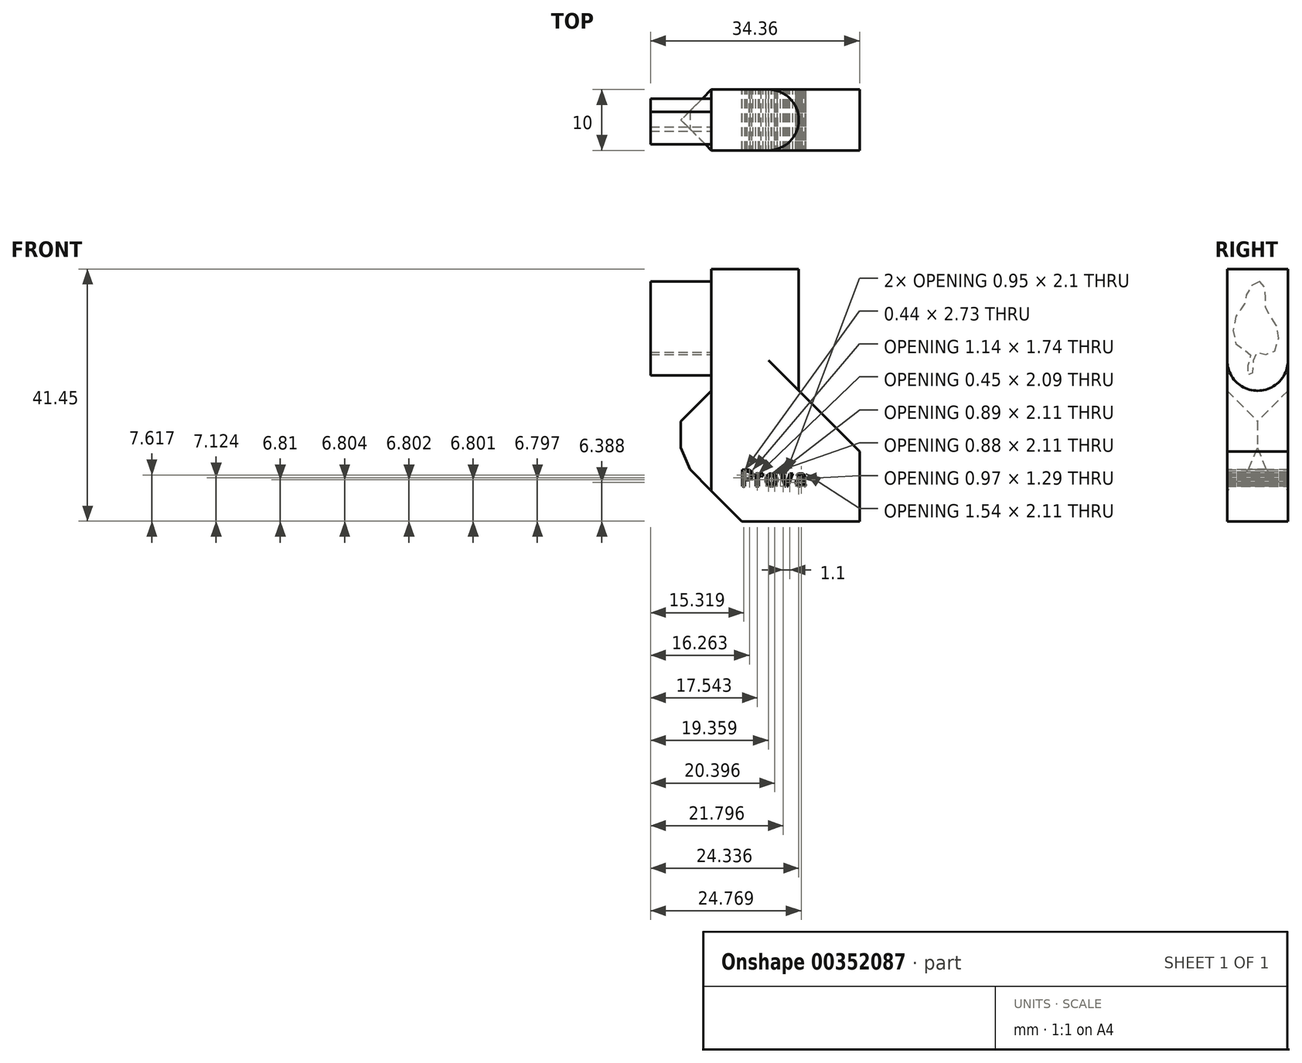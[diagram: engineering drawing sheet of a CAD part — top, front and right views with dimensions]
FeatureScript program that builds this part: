
annotation { "Feature Type Name" : "Feature", "Feature Type Description" : "" }
export const myFeature = defineFeature(function(context is Context, id is Id, definition is map)
    precondition{}
    {
        {
            var Q0;
            Q0=qCreatedBy(makeId("Front.planeOp"),FACE);
            var sketch = newSketch(context, id + "F0", { "sketchPlane" : qUnion([Q0])});
            skLineSegment(sketch, "E0.bottom", {"start": v(0, 30.39) * mm, "end": v(29.36, 30.39) * mm});
            skLineSegment(sketch, "E0.top", {"start": v(0, 8.94) * mm, "end": v(29.36, 8.94) * mm});
            skLineSegment(sketch, "E0.left", {"start": v(0, 30.39) * mm, "end": v(0, 8.94) * mm});
            skLineSegment(sketch, "E0.right", {"start": v(29.36, 30.39) * mm, "end": v(29.36, 8.94) * mm});
            skLineSegment(sketch, "E1", {"start": v(29.36, 21.93) * mm, "end": v(43.85, 8.6) * mm});
            skLineSegment(sketch, "E2", {"start": v(43.85, 8.6) * mm, "end": v(29.36, 8.94) * mm});
            skLineSegment(sketch, "E3", {"start": v(-10.64, 19.66) * mm, "end": v(0, 19.66) * mm});
            skPoint(sketch, "E3.startSnap0", {"position": v(0, 19.66) * mm});
            skLineSegment(sketch, "E4", {"start": v(0, 19.66) * mm, "end": v(-10.64, 19.66) * mm});
            skLineSegment(sketch, "E5", {"start": v(-10.64, 19.66) * mm, "end": v(-10.64, 15.53) * mm});
            skLineSegment(sketch, "E6", {"start": v(-10.64, 15.53) * mm, "end": v(-4.86, 15.53) * mm});
            skLineSegment(sketch, "E7", {"start": v(-4.86, 15.53) * mm, "end": v(-4.86, 12.5) * mm});
            skLineSegment(sketch, "E8", {"start": v(-4.86, 12.5) * mm, "end": v(-12.4, 9.66) * mm});
            skLineSegment(sketch, "E9", {"start": v(-12.4, 9.66) * mm, "end": v(0, 8.94) * mm});
            skText(sketch, "E10", { "text": "Prova", "fontName": "AllertaStencil-Regular.ttf"});
            const initialGuessF0  = {"E10": [0.00976, 0.0147, 1, 0, 0.00273]};
            skSetInitialGuess(sketch, initialGuessF0);
            skSolve(sketch);
        }
        {
            var Q0;
            {var subQ3=sQuery(id+"F0.wireOp",EDGE,"E0.bottom");Q0=makeQuery(id+"F0.imprint","IMPRINT",FACE,{"disambiguationData":[TD([[makeQuery(id+"F0.imprint","IMPRINT",EDGE,{"derivedFrom":subQ3}),-1.0]])]});}
            extrude(context, id + "F1", {"entities" : qUnion([Q0]), "depth" : 10 * mm});
        }
        {
            var Q0;
            Q0=makeQuery(id+"F1.opExtrude","SWEPT_EDGE",EDGE,{"disambiguationData":[OSD([sQuery(id+"F0.wireOp",EDGE,"E0.bottom"),sQuery(id+"F0.wireOp",EDGE,"E0.right")])]});
            chamfer(context, id + "F2", {"entities" : qUnion([Q0]), "width" : 10 * mm, "tangentPropagation" : true});
        }
        {
            var Q0;
            Q0=makeQuery(id+"F1.opExtrude","SWEPT_EDGE",EDGE,{"disambiguationData":[OSD([sQuery(id+"F0.wireOp",EDGE,"E0.top"),sQuery(id+"F0.wireOp",EDGE,"E0.left"),sQuery(id+"F0.wireOp",EDGE,"E9")])]});
            chamfer(context, id + "F3", {"entities" : qUnion([Q0]), "width" : 10 * mm, "tangentPropagation" : true});
        }
        {
            var Q0;
            Q0=makeQuery(id+"F1.opExtrude","SWEPT_FACE",FACE,{"disambiguationData":[OSD([sQuery(id+"F0.wireOp",EDGE,"E0.left")])]});
            chamfer(context, id + "F4", {"entities" : qUnion([Q0]), "width" : 5 * mm, "tangentPropagation" : true});
        }
        {
            var Q0;
            Q0=makeQuery(id+"F1.opExtrude","SWEPT_FACE",FACE,{"disambiguationData":[OSD([sQuery(id+"F0.wireOp",EDGE,"E0.bottom")])]});
            var sketch = newSketch(context, id + "F5", { "sketchPlane" : qUnion([Q0])});
            skCircle(sketch, "E11.cCircle", {"center": v(12.43, -4.86) * mm, "radius": 4.1 * mm, "construction": true});
            skLineSegment(sketch, "E11.0", {"start": v(14.52, -8.39) * mm, "end": v(10.97, -8.7) * mm});
            skLineSegment(sketch, "E11.1", {"start": v(10.97, -8.7) * mm, "end": v(8.52, -6.1) * mm});
            skLineSegment(sketch, "E11.2", {"start": v(8.52, -6.1) * mm, "end": v(9, -2.58) * mm});
            skLineSegment(sketch, "E11.3", {"start": v(9, -2.58) * mm, "end": v(12.07, -0.77) * mm});
            skLineSegment(sketch, "E11.4", {"start": v(12.07, -0.77) * mm, "end": v(15.4, -2.03) * mm});
            skLineSegment(sketch, "E11.5", {"start": v(15.4, -2.03) * mm, "end": v(16.49, -5.42) * mm});
            skLineSegment(sketch, "E11.6", {"start": v(16.49, -5.42) * mm, "end": v(14.52, -8.39) * mm});
            skSolve(sketch);
        }
        {
            var Q0;
            Q0=sQuery(id+"F5.wireOp",EDGE,"E11.1");
            var Q1;
            Q1=sQuery(id+"F5.wireOp",EDGE,"E11.0");
            var Q2;
            Q2=sQuery(id+"F5.wireOp",EDGE,"E11.6");
            var Q3;
            Q3=sQuery(id+"F5.wireOp",EDGE,"E11.5");
            var Q4;
            Q4=sQuery(id+"F5.wireOp",EDGE,"E11.4");
            var Q5;
            Q5=sQuery(id+"F5.wireOp",EDGE,"E11.3");
            var Q6;
            Q6=sQuery(id+"F5.wireOp",EDGE,"E11.2");
            extrude(context, id + "F6", {"bodyType" : ToolBodyType.SURFACE, "operationType" : NewBodyOperationType.REMOVE, "surfaceEntities" : qUnion([Q0, Q1, Q2, Q3, Q4, Q5, Q6]), "oppositeDirection" : true, "depth" : 10 * mm});
        }
        {
            var Q0;
            Q0=makeQuery(id+"F1.opExtrude","SWEPT_FACE",FACE,{"disambiguationData":[OSD([sQuery(id+"F0.wireOp",EDGE,"E0.bottom")])]});
            extrude(context, id + "F7", {"entities" : qUnion([Q0]), "operationType" : NewBodyOperationType.REMOVE, "oppositeDirection" : true, "depth" : 5 * mm});
        }
        {
            var Q0;
            Q0=makeQuery(id+"F7.boolean.opBoolean","COPY",FACE,{"derivedFrom":makeQuery(id+"F7.opExtrude","CAP_FACE",FACE,{"disambiguationData":[OSD([sQuery(id+"F0.wireOp",EDGE,"E0.bottom")])],"isStart":false})});
            extrude(context, id + "F8", {"entities" : qUnion([Q0]), "operationType" : NewBodyOperationType.ADD, "depth" : 25 * mm});
        }
        {
            var Q0;
            {var subQ0=sQuery(id+"F0.wireOp",EDGE,"E10.sketch_text.stroke-136");var subQ1=sQuery(id+"F0.wireOp",EDGE,"E10.sketch_text.stroke-135");var subQ2=sQuery(id+"F0.wireOp",EDGE,"E10.sketch_text.stroke-134");var subQ3=sQuery(id+"F0.wireOp",EDGE,"E10.sketch_text.stroke-133");var subQ4=sQuery(id+"F0.wireOp",EDGE,"E10.sketch_text.stroke-132");var subQ5=sQuery(id+"F0.wireOp",EDGE,"E10.sketch_text.stroke-131");var subQ6=sQuery(id+"F0.wireOp",EDGE,"E10.sketch_text.stroke-130");var subQ7=sQuery(id+"F0.wireOp",EDGE,"E10.sketch_text.stroke-129");var subQ8=sQuery(id+"F0.wireOp",EDGE,"E10.sketch_text.stroke-128");var subQ9=sQuery(id+"F0.wireOp",EDGE,"E10.sketch_text.stroke-127");var subQ10=sQuery(id+"F0.wireOp",EDGE,"E10.sketch_text.stroke-126");var subQ11=sQuery(id+"F0.wireOp",EDGE,"E10.sketch_text.stroke-125");var subQ12=sQuery(id+"F0.wireOp",EDGE,"E10.sketch_text.stroke-124");var subQ13=sQuery(id+"F0.wireOp",EDGE,"E10.sketch_text.stroke-123");var subQ14=sQuery(id+"F0.wireOp",EDGE,"E10.sketch_text.stroke-122");var subQ15=sQuery(id+"F0.wireOp",EDGE,"E10.sketch_text.stroke-121");var subQ16=sQuery(id+"F0.wireOp",EDGE,"E10.sketch_text.stroke-120");var subQ17=sQuery(id+"F0.wireOp",EDGE,"E10.sketch_text.stroke-119");var subQ18=sQuery(id+"F0.wireOp",EDGE,"E10.sketch_text.stroke-118");var subQ19=sQuery(id+"F0.wireOp",EDGE,"E10.sketch_text.stroke-117");var subQ20=sQuery(id+"F0.wireOp",EDGE,"E10.sketch_text.stroke-116");var subQ21=sQuery(id+"F0.wireOp",EDGE,"E10.sketch_text.stroke-115");var subQ22=sQuery(id+"F0.wireOp",EDGE,"E10.sketch_text.stroke-114");var subQ23=sQuery(id+"F0.wireOp",EDGE,"E10.sketch_text.stroke-113");var subQ24=sQuery(id+"F0.wireOp",EDGE,"E10.sketch_text.stroke-112");var subQ25=sQuery(id+"F0.wireOp",EDGE,"E10.sketch_text.stroke-111");var subQ26=sQuery(id+"F0.wireOp",EDGE,"E10.sketch_text.stroke-110");var subQ27=sQuery(id+"F0.wireOp",EDGE,"E10.sketch_text.stroke-109");var subQ28=sQuery(id+"F0.wireOp",EDGE,"E10.sketch_text.stroke-108");var subQ29=sQuery(id+"F0.wireOp",EDGE,"E10.sketch_text.stroke-107");var subQ30=sQuery(id+"F0.wireOp",EDGE,"E10.sketch_text.stroke-106");var subQ31=sQuery(id+"F0.wireOp",EDGE,"E10.sketch_text.stroke-105");var subQ32=sQuery(id+"F0.wireOp",EDGE,"E10.sketch_text.stroke-104");var subQ33=sQuery(id+"F0.wireOp",EDGE,"E10.sketch_text.stroke-103");var subQ34=sQuery(id+"F0.wireOp",EDGE,"E10.sketch_text.stroke-102");var subQ35=sQuery(id+"F0.wireOp",EDGE,"E10.sketch_text.stroke-101");var subQ36=sQuery(id+"F0.wireOp",EDGE,"E10.sketch_text.stroke-100");var subQ37=sQuery(id+"F0.wireOp",EDGE,"E10.sketch_text.stroke-99");var subQ38=sQuery(id+"F0.wireOp",EDGE,"E10.sketch_text.stroke-98");var subQ39=sQuery(id+"F0.wireOp",EDGE,"E10.sketch_text.stroke-97");var subQ40=sQuery(id+"F0.wireOp",EDGE,"E10.sketch_text.stroke-96");var subQ41=sQuery(id+"F0.wireOp",EDGE,"E10.sketch_text.stroke-95");var subQ42=sQuery(id+"F0.wireOp",EDGE,"E10.sketch_text.stroke-94");var subQ43=sQuery(id+"F0.wireOp",EDGE,"E10.sketch_text.stroke-93");var subQ44=sQuery(id+"F0.wireOp",EDGE,"E10.sketch_text.stroke-92");var subQ45=sQuery(id+"F0.wireOp",EDGE,"E10.sketch_text.stroke-91");var subQ46=sQuery(id+"F0.wireOp",EDGE,"E10.sketch_text.stroke-90");var subQ47=sQuery(id+"F0.wireOp",EDGE,"E10.sketch_text.stroke-89");var subQ48=sQuery(id+"F0.wireOp",EDGE,"E10.sketch_text.stroke-88");var subQ49=sQuery(id+"F0.wireOp",EDGE,"E10.sketch_text.stroke-87");var subQ50=sQuery(id+"F0.wireOp",EDGE,"E10.sketch_text.stroke-86");var subQ51=sQuery(id+"F0.wireOp",EDGE,"E10.sketch_text.stroke-85");var subQ52=sQuery(id+"F0.wireOp",EDGE,"E10.sketch_text.stroke-84");var subQ53=sQuery(id+"F0.wireOp",EDGE,"E10.sketch_text.stroke-83");var subQ54=sQuery(id+"F0.wireOp",EDGE,"E10.sketch_text.stroke-82");var subQ55=sQuery(id+"F0.wireOp",EDGE,"E10.sketch_text.stroke-81");var subQ56=sQuery(id+"F0.wireOp",EDGE,"E10.sketch_text.stroke-80");var subQ57=sQuery(id+"F0.wireOp",EDGE,"E10.sketch_text.stroke-79");var subQ58=sQuery(id+"F0.wireOp",EDGE,"E10.sketch_text.stroke-78");var subQ59=sQuery(id+"F0.wireOp",EDGE,"E10.sketch_text.stroke-77");var subQ60=sQuery(id+"F0.wireOp",EDGE,"E10.sketch_text.stroke-76");var subQ61=sQuery(id+"F0.wireOp",EDGE,"E10.sketch_text.stroke-75");var subQ62=sQuery(id+"F0.wireOp",EDGE,"E10.sketch_text.stroke-74");var subQ63=sQuery(id+"F0.wireOp",EDGE,"E10.sketch_text.stroke-73");var subQ64=sQuery(id+"F0.wireOp",EDGE,"E10.sketch_text.stroke-72");var subQ65=sQuery(id+"F0.wireOp",EDGE,"E10.sketch_text.stroke-71");var subQ66=sQuery(id+"F0.wireOp",EDGE,"E10.sketch_text.stroke-70");var subQ67=sQuery(id+"F0.wireOp",EDGE,"E10.sketch_text.stroke-69");var subQ68=sQuery(id+"F0.wireOp",EDGE,"E10.sketch_text.stroke-68");var subQ69=sQuery(id+"F0.wireOp",EDGE,"E10.sketch_text.stroke-67");var subQ70=sQuery(id+"F0.wireOp",EDGE,"E10.sketch_text.stroke-66");var subQ71=sQuery(id+"F0.wireOp",EDGE,"E10.sketch_text.stroke-65");var subQ72=sQuery(id+"F0.wireOp",EDGE,"E10.sketch_text.stroke-64");var subQ73=sQuery(id+"F0.wireOp",EDGE,"E10.sketch_text.stroke-63");var subQ74=sQuery(id+"F0.wireOp",EDGE,"E10.sketch_text.stroke-62");var subQ75=sQuery(id+"F0.wireOp",EDGE,"E10.sketch_text.stroke-61");var subQ76=sQuery(id+"F0.wireOp",EDGE,"E10.sketch_text.stroke-60");var subQ77=sQuery(id+"F0.wireOp",EDGE,"E10.sketch_text.stroke-59");var subQ78=sQuery(id+"F0.wireOp",EDGE,"E10.sketch_text.stroke-58");var subQ79=sQuery(id+"F0.wireOp",EDGE,"E10.sketch_text.stroke-57");var subQ80=sQuery(id+"F0.wireOp",EDGE,"E10.sketch_text.stroke-56");var subQ81=sQuery(id+"F0.wireOp",EDGE,"E10.sketch_text.stroke-55");var subQ82=sQuery(id+"F0.wireOp",EDGE,"E10.sketch_text.stroke-54");var subQ83=sQuery(id+"F0.wireOp",EDGE,"E10.sketch_text.stroke-53");var subQ84=sQuery(id+"F0.wireOp",EDGE,"E10.sketch_text.stroke-52");var subQ85=sQuery(id+"F0.wireOp",EDGE,"E10.sketch_text.stroke-51");var subQ86=sQuery(id+"F0.wireOp",EDGE,"E10.sketch_text.stroke-50");var subQ87=sQuery(id+"F0.wireOp",EDGE,"E10.sketch_text.stroke-49");var subQ88=sQuery(id+"F0.wireOp",EDGE,"E10.sketch_text.stroke-48");var subQ89=sQuery(id+"F0.wireOp",EDGE,"E10.sketch_text.stroke-47");var subQ90=sQuery(id+"F0.wireOp",EDGE,"E10.sketch_text.stroke-46");var subQ91=sQuery(id+"F0.wireOp",EDGE,"E10.sketch_text.stroke-45");var subQ92=sQuery(id+"F0.wireOp",EDGE,"E10.sketch_text.stroke-44");var subQ93=sQuery(id+"F0.wireOp",EDGE,"E10.sketch_text.stroke-43");var subQ94=sQuery(id+"F0.wireOp",EDGE,"E10.sketch_text.stroke-42");var subQ95=sQuery(id+"F0.wireOp",EDGE,"E10.sketch_text.stroke-41");var subQ96=sQuery(id+"F0.wireOp",EDGE,"E10.sketch_text.stroke-40");var subQ97=sQuery(id+"F0.wireOp",EDGE,"E10.sketch_text.stroke-39");var subQ98=sQuery(id+"F0.wireOp",EDGE,"E10.sketch_text.stroke-38");var subQ99=sQuery(id+"F0.wireOp",EDGE,"E10.sketch_text.stroke-37");var subQ100=sQuery(id+"F0.wireOp",EDGE,"E10.sketch_text.stroke-36");var subQ101=sQuery(id+"F0.wireOp",EDGE,"E10.sketch_text.stroke-35");var subQ102=sQuery(id+"F0.wireOp",EDGE,"E10.sketch_text.stroke-34");var subQ103=sQuery(id+"F0.wireOp",EDGE,"E10.sketch_text.stroke-33");var subQ104=sQuery(id+"F0.wireOp",EDGE,"E10.sketch_text.stroke-32");var subQ105=sQuery(id+"F0.wireOp",EDGE,"E10.sketch_text.stroke-31");var subQ106=sQuery(id+"F0.wireOp",EDGE,"E10.sketch_text.stroke-30");var subQ107=sQuery(id+"F0.wireOp",EDGE,"E10.sketch_text.stroke-29");var subQ108=sQuery(id+"F0.wireOp",EDGE,"E10.sketch_text.stroke-28");var subQ109=sQuery(id+"F0.wireOp",EDGE,"E10.sketch_text.stroke-27");var subQ110=sQuery(id+"F0.wireOp",EDGE,"E10.sketch_text.stroke-26");var subQ111=sQuery(id+"F0.wireOp",EDGE,"E10.sketch_text.stroke-25");var subQ112=sQuery(id+"F0.wireOp",EDGE,"E10.sketch_text.stroke-24");var subQ113=sQuery(id+"F0.wireOp",EDGE,"E10.sketch_text.stroke-23");var subQ114=sQuery(id+"F0.wireOp",EDGE,"E10.sketch_text.stroke-22");var subQ115=sQuery(id+"F0.wireOp",EDGE,"E10.sketch_text.stroke-21");var subQ116=sQuery(id+"F0.wireOp",EDGE,"E10.sketch_text.stroke-20");var subQ117=sQuery(id+"F0.wireOp",EDGE,"E10.sketch_text.stroke-19");var subQ118=sQuery(id+"F0.wireOp",EDGE,"E10.sketch_text.stroke-18");var subQ119=sQuery(id+"F0.wireOp",EDGE,"E10.sketch_text.stroke-17");var subQ120=sQuery(id+"F0.wireOp",EDGE,"E10.sketch_text.stroke-16");var subQ121=sQuery(id+"F0.wireOp",EDGE,"E10.sketch_text.stroke-15");var subQ122=sQuery(id+"F0.wireOp",EDGE,"E10.sketch_text.stroke-14");var subQ123=sQuery(id+"F0.wireOp",EDGE,"E10.sketch_text.stroke-13");var subQ124=sQuery(id+"F0.wireOp",EDGE,"E10.sketch_text.stroke-12");var subQ125=sQuery(id+"F0.wireOp",EDGE,"E10.sketch_text.stroke-11");var subQ126=sQuery(id+"F0.wireOp",EDGE,"E10.sketch_text.stroke-10");var subQ127=sQuery(id+"F0.wireOp",EDGE,"E10.sketch_text.stroke-9");var subQ128=sQuery(id+"F0.wireOp",EDGE,"E10.sketch_text.stroke-8");var subQ129=sQuery(id+"F0.wireOp",EDGE,"E10.sketch_text.stroke-7");var subQ130=sQuery(id+"F0.wireOp",EDGE,"E10.sketch_text.stroke-6");var subQ131=sQuery(id+"F0.wireOp",EDGE,"E10.sketch_text.stroke-5");var subQ132=sQuery(id+"F0.wireOp",EDGE,"E10.sketch_text.stroke-4");var subQ133=sQuery(id+"F0.wireOp",EDGE,"E10.sketch_text.stroke-3");var subQ134=sQuery(id+"F0.wireOp",EDGE,"E10.sketch_text.stroke-2");var subQ135=sQuery(id+"F0.wireOp",EDGE,"E10.sketch_text.stroke-1");var subQ136=sQuery(id+"F0.wireOp",EDGE,"E10.sketch_text.stroke-0");var subQ137=sQuery(id+"F0.wireOp",EDGE,"E0.right");var subQ138=sQuery(id+"F0.wireOp",EDGE,"E0.left");var subQ139=sQuery(id+"F0.wireOp",EDGE,"E0.top");var subQ140=sQuery(id+"F0.wireOp",EDGE,"E0.bottom");Q0=makeQuery(id+"F8.opExtrude","SWEPT_EDGE",EDGE,{"disambiguationData":[OSD([subQ140,subQ139,subQ138,subQ137,subQ136,subQ135,subQ134,subQ133,subQ132,subQ131,subQ130,subQ129,subQ128,subQ127,subQ126,subQ125,subQ124,subQ123,subQ122,subQ121,subQ120,subQ119,subQ118,subQ117,subQ116,subQ115,subQ114,subQ113,subQ112,subQ111,subQ110,subQ109,subQ108,subQ107,subQ106,subQ105,subQ104,subQ103,subQ102,subQ101,subQ100,subQ99,subQ98,subQ97,subQ96,subQ95,subQ94,subQ93,subQ92,subQ91,subQ90,subQ89,subQ88,subQ87,subQ86,subQ85,subQ84,subQ83,subQ82,subQ81,subQ80,subQ79,subQ78,subQ77,subQ76,subQ75,subQ74,subQ73,subQ72,subQ71,subQ70,subQ69,subQ68,subQ67,subQ66,subQ65,subQ64,subQ63,subQ62,subQ61,subQ60,subQ59,subQ58,subQ57,subQ56,subQ55,subQ54,subQ53,subQ52,subQ51,subQ50,subQ49,subQ48,subQ47,subQ46,subQ45,subQ44,subQ43,subQ42,subQ41,subQ40,subQ39,subQ38,subQ37,subQ36,subQ35,subQ34,subQ33,subQ32,subQ31,subQ30,subQ29,subQ28,subQ27,subQ26,subQ25,subQ24,subQ23,subQ22,subQ21,subQ20,subQ19,subQ18,subQ17,subQ16,subQ15,subQ14,subQ13,subQ12,subQ11,subQ10,subQ9,subQ8,subQ7,subQ6,subQ5,subQ4,subQ3,subQ2,subQ1,subQ0]),TDD([makeQuery(id+"F7.boolean.opBoolean","COPY",VERTEX,{"derivedFrom":makeQuery(id+"F7.opExtrude","CAP_VERTEX",VERTEX,{"disambiguationData":[OSD([subQ140,subQ139,subQ138,subQ137,subQ136,subQ135,subQ134,subQ133,subQ132,subQ131,subQ130,subQ129,subQ128,subQ127,subQ126,subQ125,subQ124,subQ123,subQ122,subQ121,subQ120,subQ119,subQ118,subQ117,subQ116,subQ115,subQ114,subQ113,subQ112,subQ111,subQ110,subQ109,subQ108,subQ107,subQ106,subQ105,subQ104,subQ103,subQ102,subQ101,subQ100,subQ99,subQ98,subQ97,subQ96,subQ95,subQ94,subQ93,subQ92,subQ91,subQ90,subQ89,subQ88,subQ87,subQ86,subQ85,subQ84,subQ83,subQ82,subQ81,subQ80,subQ79,subQ78,subQ77,subQ76,subQ75,subQ74,subQ73,subQ72,subQ71,subQ70,subQ69,subQ68,subQ67,subQ66,subQ65,subQ64,subQ63,subQ62,subQ61,subQ60,subQ59,subQ58,subQ57,subQ56,subQ55,subQ54,subQ53,subQ52,subQ51,subQ50,subQ49,subQ48,subQ47,subQ46,subQ45,subQ44,subQ43,subQ42,subQ41,subQ40,subQ39,subQ38,subQ37,subQ36,subQ35,subQ34,subQ33,subQ32,subQ31,subQ30,subQ29,subQ28,subQ27,subQ26,subQ25,subQ24,subQ23,subQ22,subQ21,subQ20,subQ19,subQ18,subQ17,subQ16,subQ15,subQ14,subQ13,subQ12,subQ11,subQ10,subQ9,subQ8,subQ7,subQ6,subQ5,subQ4,subQ3,subQ2,subQ1,subQ0]),TDD([makeQuery(id+"F2.opChamfer","BLEND_VERTEX",VERTEX,{"blendedFrom":[makeQuery(id+"F1.opExtrude","SWEPT_EDGE",EDGE,{"disambiguationData":[OSD([subQ140,subQ137])]}),makeQuery(id+"F1.opExtrude","SWEPT_FACE",FACE,{"disambiguationData":[OSD([subQ140])]}),makeQuery(id+"F1.opExtrude","CAP_FACE",FACE,{"disambiguationData":[OSD([subQ140,subQ139,subQ138,subQ137,subQ136,subQ135,subQ134,subQ133,subQ132,subQ131,subQ130,subQ129,subQ128,subQ127,subQ126,subQ125,subQ124,subQ123,subQ122,subQ121,subQ120,subQ119,subQ118,subQ117,subQ116,subQ115,subQ114,subQ113,subQ112,subQ111,subQ110,subQ109,subQ108,subQ107,subQ106,subQ105,subQ104,subQ103,subQ102,subQ101,subQ100,subQ99,subQ98,subQ97,subQ96,subQ95,subQ94,subQ93,subQ92,subQ91,subQ90,subQ89,subQ88,subQ87,subQ86,subQ85,subQ84,subQ83,subQ82,subQ81,subQ80,subQ79,subQ78,subQ77,subQ76,subQ75,subQ74,subQ73,subQ72,subQ71,subQ70,subQ69,subQ68,subQ67,subQ66,subQ65,subQ64,subQ63,subQ62,subQ61,subQ60,subQ59,subQ58,subQ57,subQ56,subQ55,subQ54,subQ53,subQ52,subQ51,subQ50,subQ49,subQ48,subQ47,subQ46,subQ45,subQ44,subQ43,subQ42,subQ41,subQ40,subQ39,subQ38,subQ37,subQ36,subQ35,subQ34,subQ33,subQ32,subQ31,subQ30,subQ29,subQ28,subQ27,subQ26,subQ25,subQ24,subQ23,subQ22,subQ21,subQ20,subQ19,subQ18,subQ17,subQ16,subQ15,subQ14,subQ13,subQ12,subQ11,subQ10,subQ9,subQ8,subQ7,subQ6,subQ5,subQ4,subQ3,subQ2,subQ1,subQ0])],"isStart":false})],"blendedInto":[makeQuery(id+"F1.opExtrude","SWEPT_FACE",FACE,{"disambiguationData":[OSD([subQ140])]}),makeQuery(id+"F1.opExtrude","CAP_FACE",FACE,{"disambiguationData":[OSD([subQ140,subQ139,subQ138,subQ137,subQ136,subQ135,subQ134,subQ133,subQ132,subQ131,subQ130,subQ129,subQ128,subQ127,subQ126,subQ125,subQ124,subQ123,subQ122,subQ121,subQ120,subQ119,subQ118,subQ117,subQ116,subQ115,subQ114,subQ113,subQ112,subQ111,subQ110,subQ109,subQ108,subQ107,subQ106,subQ105,subQ104,subQ103,subQ102,subQ101,subQ100,subQ99,subQ98,subQ97,subQ96,subQ95,subQ94,subQ93,subQ92,subQ91,subQ90,subQ89,subQ88,subQ87,subQ86,subQ85,subQ84,subQ83,subQ82,subQ81,subQ80,subQ79,subQ78,subQ77,subQ76,subQ75,subQ74,subQ73,subQ72,subQ71,subQ70,subQ69,subQ68,subQ67,subQ66,subQ65,subQ64,subQ63,subQ62,subQ61,subQ60,subQ59,subQ58,subQ57,subQ56,subQ55,subQ54,subQ53,subQ52,subQ51,subQ50,subQ49,subQ48,subQ47,subQ46,subQ45,subQ44,subQ43,subQ42,subQ41,subQ40,subQ39,subQ38,subQ37,subQ36,subQ35,subQ34,subQ33,subQ32,subQ31,subQ30,subQ29,subQ28,subQ27,subQ26,subQ25,subQ24,subQ23,subQ22,subQ21,subQ20,subQ19,subQ18,subQ17,subQ16,subQ15,subQ14,subQ13,subQ12,subQ11,subQ10,subQ9,subQ8,subQ7,subQ6,subQ5,subQ4,subQ3,subQ2,subQ1,subQ0])],"isStart":false})]})])],"isStart":false})})])]});}
            fillet(context, id + "F9", {"entities" : qUnion([Q0]), "radius" : 5 * mm, "tangentPropagation" : true, "allowEdgeOverflow" : false});
        }
        {
            var Q0;
            {var subQ0=sQuery(id+"F0.wireOp",EDGE,"E10.sketch_text.stroke-136");var subQ1=sQuery(id+"F0.wireOp",EDGE,"E10.sketch_text.stroke-135");var subQ2=sQuery(id+"F0.wireOp",EDGE,"E10.sketch_text.stroke-134");var subQ3=sQuery(id+"F0.wireOp",EDGE,"E10.sketch_text.stroke-133");var subQ4=sQuery(id+"F0.wireOp",EDGE,"E10.sketch_text.stroke-132");var subQ5=sQuery(id+"F0.wireOp",EDGE,"E10.sketch_text.stroke-131");var subQ6=sQuery(id+"F0.wireOp",EDGE,"E10.sketch_text.stroke-130");var subQ7=sQuery(id+"F0.wireOp",EDGE,"E10.sketch_text.stroke-129");var subQ8=sQuery(id+"F0.wireOp",EDGE,"E10.sketch_text.stroke-128");var subQ9=sQuery(id+"F0.wireOp",EDGE,"E10.sketch_text.stroke-127");var subQ10=sQuery(id+"F0.wireOp",EDGE,"E10.sketch_text.stroke-126");var subQ11=sQuery(id+"F0.wireOp",EDGE,"E10.sketch_text.stroke-125");var subQ12=sQuery(id+"F0.wireOp",EDGE,"E10.sketch_text.stroke-124");var subQ13=sQuery(id+"F0.wireOp",EDGE,"E10.sketch_text.stroke-123");var subQ14=sQuery(id+"F0.wireOp",EDGE,"E10.sketch_text.stroke-122");var subQ15=sQuery(id+"F0.wireOp",EDGE,"E10.sketch_text.stroke-121");var subQ16=sQuery(id+"F0.wireOp",EDGE,"E10.sketch_text.stroke-120");var subQ17=sQuery(id+"F0.wireOp",EDGE,"E10.sketch_text.stroke-119");var subQ18=sQuery(id+"F0.wireOp",EDGE,"E10.sketch_text.stroke-118");var subQ19=sQuery(id+"F0.wireOp",EDGE,"E10.sketch_text.stroke-117");var subQ20=sQuery(id+"F0.wireOp",EDGE,"E10.sketch_text.stroke-116");var subQ21=sQuery(id+"F0.wireOp",EDGE,"E10.sketch_text.stroke-115");var subQ22=sQuery(id+"F0.wireOp",EDGE,"E10.sketch_text.stroke-114");var subQ23=sQuery(id+"F0.wireOp",EDGE,"E10.sketch_text.stroke-113");var subQ24=sQuery(id+"F0.wireOp",EDGE,"E10.sketch_text.stroke-112");var subQ25=sQuery(id+"F0.wireOp",EDGE,"E10.sketch_text.stroke-111");var subQ26=sQuery(id+"F0.wireOp",EDGE,"E10.sketch_text.stroke-110");var subQ27=sQuery(id+"F0.wireOp",EDGE,"E10.sketch_text.stroke-109");var subQ28=sQuery(id+"F0.wireOp",EDGE,"E10.sketch_text.stroke-108");var subQ29=sQuery(id+"F0.wireOp",EDGE,"E10.sketch_text.stroke-107");var subQ30=sQuery(id+"F0.wireOp",EDGE,"E10.sketch_text.stroke-106");var subQ31=sQuery(id+"F0.wireOp",EDGE,"E10.sketch_text.stroke-105");var subQ32=sQuery(id+"F0.wireOp",EDGE,"E10.sketch_text.stroke-104");var subQ33=sQuery(id+"F0.wireOp",EDGE,"E10.sketch_text.stroke-103");var subQ34=sQuery(id+"F0.wireOp",EDGE,"E10.sketch_text.stroke-102");var subQ35=sQuery(id+"F0.wireOp",EDGE,"E10.sketch_text.stroke-101");var subQ36=sQuery(id+"F0.wireOp",EDGE,"E10.sketch_text.stroke-100");var subQ37=sQuery(id+"F0.wireOp",EDGE,"E10.sketch_text.stroke-99");var subQ38=sQuery(id+"F0.wireOp",EDGE,"E10.sketch_text.stroke-98");var subQ39=sQuery(id+"F0.wireOp",EDGE,"E10.sketch_text.stroke-97");var subQ40=sQuery(id+"F0.wireOp",EDGE,"E10.sketch_text.stroke-96");var subQ41=sQuery(id+"F0.wireOp",EDGE,"E10.sketch_text.stroke-95");var subQ42=sQuery(id+"F0.wireOp",EDGE,"E10.sketch_text.stroke-94");var subQ43=sQuery(id+"F0.wireOp",EDGE,"E10.sketch_text.stroke-93");var subQ44=sQuery(id+"F0.wireOp",EDGE,"E10.sketch_text.stroke-92");var subQ45=sQuery(id+"F0.wireOp",EDGE,"E10.sketch_text.stroke-91");var subQ46=sQuery(id+"F0.wireOp",EDGE,"E10.sketch_text.stroke-90");var subQ47=sQuery(id+"F0.wireOp",EDGE,"E10.sketch_text.stroke-89");var subQ48=sQuery(id+"F0.wireOp",EDGE,"E10.sketch_text.stroke-88");var subQ49=sQuery(id+"F0.wireOp",EDGE,"E10.sketch_text.stroke-87");var subQ50=sQuery(id+"F0.wireOp",EDGE,"E10.sketch_text.stroke-86");var subQ51=sQuery(id+"F0.wireOp",EDGE,"E10.sketch_text.stroke-85");var subQ52=sQuery(id+"F0.wireOp",EDGE,"E10.sketch_text.stroke-84");var subQ53=sQuery(id+"F0.wireOp",EDGE,"E10.sketch_text.stroke-83");var subQ54=sQuery(id+"F0.wireOp",EDGE,"E10.sketch_text.stroke-82");var subQ55=sQuery(id+"F0.wireOp",EDGE,"E10.sketch_text.stroke-81");var subQ56=sQuery(id+"F0.wireOp",EDGE,"E10.sketch_text.stroke-80");var subQ57=sQuery(id+"F0.wireOp",EDGE,"E10.sketch_text.stroke-79");var subQ58=sQuery(id+"F0.wireOp",EDGE,"E10.sketch_text.stroke-78");var subQ59=sQuery(id+"F0.wireOp",EDGE,"E10.sketch_text.stroke-77");var subQ60=sQuery(id+"F0.wireOp",EDGE,"E10.sketch_text.stroke-76");var subQ61=sQuery(id+"F0.wireOp",EDGE,"E10.sketch_text.stroke-75");var subQ62=sQuery(id+"F0.wireOp",EDGE,"E10.sketch_text.stroke-74");var subQ63=sQuery(id+"F0.wireOp",EDGE,"E10.sketch_text.stroke-73");var subQ64=sQuery(id+"F0.wireOp",EDGE,"E10.sketch_text.stroke-72");var subQ65=sQuery(id+"F0.wireOp",EDGE,"E10.sketch_text.stroke-71");var subQ66=sQuery(id+"F0.wireOp",EDGE,"E10.sketch_text.stroke-70");var subQ67=sQuery(id+"F0.wireOp",EDGE,"E10.sketch_text.stroke-69");var subQ68=sQuery(id+"F0.wireOp",EDGE,"E10.sketch_text.stroke-68");var subQ69=sQuery(id+"F0.wireOp",EDGE,"E10.sketch_text.stroke-67");var subQ70=sQuery(id+"F0.wireOp",EDGE,"E10.sketch_text.stroke-66");var subQ71=sQuery(id+"F0.wireOp",EDGE,"E10.sketch_text.stroke-65");var subQ72=sQuery(id+"F0.wireOp",EDGE,"E10.sketch_text.stroke-64");var subQ73=sQuery(id+"F0.wireOp",EDGE,"E10.sketch_text.stroke-63");var subQ74=sQuery(id+"F0.wireOp",EDGE,"E10.sketch_text.stroke-62");var subQ75=sQuery(id+"F0.wireOp",EDGE,"E10.sketch_text.stroke-61");var subQ76=sQuery(id+"F0.wireOp",EDGE,"E10.sketch_text.stroke-60");var subQ77=sQuery(id+"F0.wireOp",EDGE,"E10.sketch_text.stroke-59");var subQ78=sQuery(id+"F0.wireOp",EDGE,"E10.sketch_text.stroke-58");var subQ79=sQuery(id+"F0.wireOp",EDGE,"E10.sketch_text.stroke-57");var subQ80=sQuery(id+"F0.wireOp",EDGE,"E10.sketch_text.stroke-56");var subQ81=sQuery(id+"F0.wireOp",EDGE,"E10.sketch_text.stroke-55");var subQ82=sQuery(id+"F0.wireOp",EDGE,"E10.sketch_text.stroke-54");var subQ83=sQuery(id+"F0.wireOp",EDGE,"E10.sketch_text.stroke-53");var subQ84=sQuery(id+"F0.wireOp",EDGE,"E10.sketch_text.stroke-52");var subQ85=sQuery(id+"F0.wireOp",EDGE,"E10.sketch_text.stroke-51");var subQ86=sQuery(id+"F0.wireOp",EDGE,"E10.sketch_text.stroke-50");var subQ87=sQuery(id+"F0.wireOp",EDGE,"E10.sketch_text.stroke-49");var subQ88=sQuery(id+"F0.wireOp",EDGE,"E10.sketch_text.stroke-48");var subQ89=sQuery(id+"F0.wireOp",EDGE,"E10.sketch_text.stroke-47");var subQ90=sQuery(id+"F0.wireOp",EDGE,"E10.sketch_text.stroke-46");var subQ91=sQuery(id+"F0.wireOp",EDGE,"E10.sketch_text.stroke-45");var subQ92=sQuery(id+"F0.wireOp",EDGE,"E10.sketch_text.stroke-44");var subQ93=sQuery(id+"F0.wireOp",EDGE,"E10.sketch_text.stroke-43");var subQ94=sQuery(id+"F0.wireOp",EDGE,"E10.sketch_text.stroke-42");var subQ95=sQuery(id+"F0.wireOp",EDGE,"E10.sketch_text.stroke-41");var subQ96=sQuery(id+"F0.wireOp",EDGE,"E10.sketch_text.stroke-40");var subQ97=sQuery(id+"F0.wireOp",EDGE,"E10.sketch_text.stroke-39");var subQ98=sQuery(id+"F0.wireOp",EDGE,"E10.sketch_text.stroke-38");var subQ99=sQuery(id+"F0.wireOp",EDGE,"E10.sketch_text.stroke-37");var subQ100=sQuery(id+"F0.wireOp",EDGE,"E10.sketch_text.stroke-36");var subQ101=sQuery(id+"F0.wireOp",EDGE,"E10.sketch_text.stroke-35");var subQ102=sQuery(id+"F0.wireOp",EDGE,"E10.sketch_text.stroke-34");var subQ103=sQuery(id+"F0.wireOp",EDGE,"E10.sketch_text.stroke-33");var subQ104=sQuery(id+"F0.wireOp",EDGE,"E10.sketch_text.stroke-32");var subQ105=sQuery(id+"F0.wireOp",EDGE,"E10.sketch_text.stroke-31");var subQ106=sQuery(id+"F0.wireOp",EDGE,"E10.sketch_text.stroke-30");var subQ107=sQuery(id+"F0.wireOp",EDGE,"E10.sketch_text.stroke-29");var subQ108=sQuery(id+"F0.wireOp",EDGE,"E10.sketch_text.stroke-28");var subQ109=sQuery(id+"F0.wireOp",EDGE,"E10.sketch_text.stroke-27");var subQ110=sQuery(id+"F0.wireOp",EDGE,"E10.sketch_text.stroke-26");var subQ111=sQuery(id+"F0.wireOp",EDGE,"E10.sketch_text.stroke-25");var subQ112=sQuery(id+"F0.wireOp",EDGE,"E10.sketch_text.stroke-24");var subQ113=sQuery(id+"F0.wireOp",EDGE,"E10.sketch_text.stroke-23");var subQ114=sQuery(id+"F0.wireOp",EDGE,"E10.sketch_text.stroke-22");var subQ115=sQuery(id+"F0.wireOp",EDGE,"E10.sketch_text.stroke-21");var subQ116=sQuery(id+"F0.wireOp",EDGE,"E10.sketch_text.stroke-20");var subQ117=sQuery(id+"F0.wireOp",EDGE,"E10.sketch_text.stroke-19");var subQ118=sQuery(id+"F0.wireOp",EDGE,"E10.sketch_text.stroke-18");var subQ119=sQuery(id+"F0.wireOp",EDGE,"E10.sketch_text.stroke-17");var subQ120=sQuery(id+"F0.wireOp",EDGE,"E10.sketch_text.stroke-16");var subQ121=sQuery(id+"F0.wireOp",EDGE,"E10.sketch_text.stroke-15");var subQ122=sQuery(id+"F0.wireOp",EDGE,"E10.sketch_text.stroke-14");var subQ123=sQuery(id+"F0.wireOp",EDGE,"E10.sketch_text.stroke-13");var subQ124=sQuery(id+"F0.wireOp",EDGE,"E10.sketch_text.stroke-12");var subQ125=sQuery(id+"F0.wireOp",EDGE,"E10.sketch_text.stroke-11");var subQ126=sQuery(id+"F0.wireOp",EDGE,"E10.sketch_text.stroke-10");var subQ127=sQuery(id+"F0.wireOp",EDGE,"E10.sketch_text.stroke-9");var subQ128=sQuery(id+"F0.wireOp",EDGE,"E10.sketch_text.stroke-8");var subQ129=sQuery(id+"F0.wireOp",EDGE,"E10.sketch_text.stroke-7");var subQ130=sQuery(id+"F0.wireOp",EDGE,"E10.sketch_text.stroke-6");var subQ131=sQuery(id+"F0.wireOp",EDGE,"E10.sketch_text.stroke-5");var subQ132=sQuery(id+"F0.wireOp",EDGE,"E10.sketch_text.stroke-4");var subQ133=sQuery(id+"F0.wireOp",EDGE,"E10.sketch_text.stroke-3");var subQ134=sQuery(id+"F0.wireOp",EDGE,"E10.sketch_text.stroke-2");var subQ135=sQuery(id+"F0.wireOp",EDGE,"E10.sketch_text.stroke-1");var subQ136=sQuery(id+"F0.wireOp",EDGE,"E10.sketch_text.stroke-0");var subQ137=sQuery(id+"F0.wireOp",EDGE,"E0.right");var subQ138=sQuery(id+"F0.wireOp",EDGE,"E0.left");var subQ139=sQuery(id+"F0.wireOp",EDGE,"E0.top");var subQ140=sQuery(id+"F0.wireOp",EDGE,"E0.bottom");Q0=makeQuery(id+"F8.opExtrude","SWEPT_EDGE",EDGE,{"disambiguationData":[OSD([subQ140,subQ139,subQ138,subQ137,subQ136,subQ135,subQ134,subQ133,subQ132,subQ131,subQ130,subQ129,subQ128,subQ127,subQ126,subQ125,subQ124,subQ123,subQ122,subQ121,subQ120,subQ119,subQ118,subQ117,subQ116,subQ115,subQ114,subQ113,subQ112,subQ111,subQ110,subQ109,subQ108,subQ107,subQ106,subQ105,subQ104,subQ103,subQ102,subQ101,subQ100,subQ99,subQ98,subQ97,subQ96,subQ95,subQ94,subQ93,subQ92,subQ91,subQ90,subQ89,subQ88,subQ87,subQ86,subQ85,subQ84,subQ83,subQ82,subQ81,subQ80,subQ79,subQ78,subQ77,subQ76,subQ75,subQ74,subQ73,subQ72,subQ71,subQ70,subQ69,subQ68,subQ67,subQ66,subQ65,subQ64,subQ63,subQ62,subQ61,subQ60,subQ59,subQ58,subQ57,subQ56,subQ55,subQ54,subQ53,subQ52,subQ51,subQ50,subQ49,subQ48,subQ47,subQ46,subQ45,subQ44,subQ43,subQ42,subQ41,subQ40,subQ39,subQ38,subQ37,subQ36,subQ35,subQ34,subQ33,subQ32,subQ31,subQ30,subQ29,subQ28,subQ27,subQ26,subQ25,subQ24,subQ23,subQ22,subQ21,subQ20,subQ19,subQ18,subQ17,subQ16,subQ15,subQ14,subQ13,subQ12,subQ11,subQ10,subQ9,subQ8,subQ7,subQ6,subQ5,subQ4,subQ3,subQ2,subQ1,subQ0]),TDD([makeQuery(id+"F7.boolean.opBoolean","COPY",VERTEX,{"derivedFrom":makeQuery(id+"F7.opExtrude","CAP_VERTEX",VERTEX,{"disambiguationData":[OSD([subQ140,subQ139,subQ138,subQ137,subQ136,subQ135,subQ134,subQ133,subQ132,subQ131,subQ130,subQ129,subQ128,subQ127,subQ126,subQ125,subQ124,subQ123,subQ122,subQ121,subQ120,subQ119,subQ118,subQ117,subQ116,subQ115,subQ114,subQ113,subQ112,subQ111,subQ110,subQ109,subQ108,subQ107,subQ106,subQ105,subQ104,subQ103,subQ102,subQ101,subQ100,subQ99,subQ98,subQ97,subQ96,subQ95,subQ94,subQ93,subQ92,subQ91,subQ90,subQ89,subQ88,subQ87,subQ86,subQ85,subQ84,subQ83,subQ82,subQ81,subQ80,subQ79,subQ78,subQ77,subQ76,subQ75,subQ74,subQ73,subQ72,subQ71,subQ70,subQ69,subQ68,subQ67,subQ66,subQ65,subQ64,subQ63,subQ62,subQ61,subQ60,subQ59,subQ58,subQ57,subQ56,subQ55,subQ54,subQ53,subQ52,subQ51,subQ50,subQ49,subQ48,subQ47,subQ46,subQ45,subQ44,subQ43,subQ42,subQ41,subQ40,subQ39,subQ38,subQ37,subQ36,subQ35,subQ34,subQ33,subQ32,subQ31,subQ30,subQ29,subQ28,subQ27,subQ26,subQ25,subQ24,subQ23,subQ22,subQ21,subQ20,subQ19,subQ18,subQ17,subQ16,subQ15,subQ14,subQ13,subQ12,subQ11,subQ10,subQ9,subQ8,subQ7,subQ6,subQ5,subQ4,subQ3,subQ2,subQ1,subQ0]),TDD([makeQuery(id+"F2.opChamfer","BLEND_VERTEX",VERTEX,{"blendedFrom":[makeQuery(id+"F1.opExtrude","SWEPT_EDGE",EDGE,{"disambiguationData":[OSD([subQ140,subQ137])]}),makeQuery(id+"F1.opExtrude","SWEPT_FACE",FACE,{"disambiguationData":[OSD([subQ140])]}),makeQuery(id+"F1.opExtrude","CAP_FACE",FACE,{"disambiguationData":[OSD([subQ140,subQ139,subQ138,subQ137,subQ136,subQ135,subQ134,subQ133,subQ132,subQ131,subQ130,subQ129,subQ128,subQ127,subQ126,subQ125,subQ124,subQ123,subQ122,subQ121,subQ120,subQ119,subQ118,subQ117,subQ116,subQ115,subQ114,subQ113,subQ112,subQ111,subQ110,subQ109,subQ108,subQ107,subQ106,subQ105,subQ104,subQ103,subQ102,subQ101,subQ100,subQ99,subQ98,subQ97,subQ96,subQ95,subQ94,subQ93,subQ92,subQ91,subQ90,subQ89,subQ88,subQ87,subQ86,subQ85,subQ84,subQ83,subQ82,subQ81,subQ80,subQ79,subQ78,subQ77,subQ76,subQ75,subQ74,subQ73,subQ72,subQ71,subQ70,subQ69,subQ68,subQ67,subQ66,subQ65,subQ64,subQ63,subQ62,subQ61,subQ60,subQ59,subQ58,subQ57,subQ56,subQ55,subQ54,subQ53,subQ52,subQ51,subQ50,subQ49,subQ48,subQ47,subQ46,subQ45,subQ44,subQ43,subQ42,subQ41,subQ40,subQ39,subQ38,subQ37,subQ36,subQ35,subQ34,subQ33,subQ32,subQ31,subQ30,subQ29,subQ28,subQ27,subQ26,subQ25,subQ24,subQ23,subQ22,subQ21,subQ20,subQ19,subQ18,subQ17,subQ16,subQ15,subQ14,subQ13,subQ12,subQ11,subQ10,subQ9,subQ8,subQ7,subQ6,subQ5,subQ4,subQ3,subQ2,subQ1,subQ0])],"isStart":true})],"blendedInto":[makeQuery(id+"F1.opExtrude","SWEPT_FACE",FACE,{"disambiguationData":[OSD([subQ140])]}),makeQuery(id+"F1.opExtrude","CAP_FACE",FACE,{"disambiguationData":[OSD([subQ140,subQ139,subQ138,subQ137,subQ136,subQ135,subQ134,subQ133,subQ132,subQ131,subQ130,subQ129,subQ128,subQ127,subQ126,subQ125,subQ124,subQ123,subQ122,subQ121,subQ120,subQ119,subQ118,subQ117,subQ116,subQ115,subQ114,subQ113,subQ112,subQ111,subQ110,subQ109,subQ108,subQ107,subQ106,subQ105,subQ104,subQ103,subQ102,subQ101,subQ100,subQ99,subQ98,subQ97,subQ96,subQ95,subQ94,subQ93,subQ92,subQ91,subQ90,subQ89,subQ88,subQ87,subQ86,subQ85,subQ84,subQ83,subQ82,subQ81,subQ80,subQ79,subQ78,subQ77,subQ76,subQ75,subQ74,subQ73,subQ72,subQ71,subQ70,subQ69,subQ68,subQ67,subQ66,subQ65,subQ64,subQ63,subQ62,subQ61,subQ60,subQ59,subQ58,subQ57,subQ56,subQ55,subQ54,subQ53,subQ52,subQ51,subQ50,subQ49,subQ48,subQ47,subQ46,subQ45,subQ44,subQ43,subQ42,subQ41,subQ40,subQ39,subQ38,subQ37,subQ36,subQ35,subQ34,subQ33,subQ32,subQ31,subQ30,subQ29,subQ28,subQ27,subQ26,subQ25,subQ24,subQ23,subQ22,subQ21,subQ20,subQ19,subQ18,subQ17,subQ16,subQ15,subQ14,subQ13,subQ12,subQ11,subQ10,subQ9,subQ8,subQ7,subQ6,subQ5,subQ4,subQ3,subQ2,subQ1,subQ0])],"isStart":true})]})])],"isStart":false})})])]});}
            fillet(context, id + "F10", {"entities" : qUnion([Q0]), "radius" : 5 * mm, "tangentPropagation" : true, "allowEdgeOverflow" : false});
        }
        {
            var Q0;
            Q0=makeQuery(id+"F8.opExtrude","SWEPT_FACE",FACE,{"disambiguationData":[OSD([sQuery(id+"F0.wireOp",EDGE,"E0.bottom"),sQuery(id+"F0.wireOp",EDGE,"E0.left")])]});
            var sketch = newSketch(context, id + "F11", { "sketchPlane" : qUnion([Q0])});
            skPoint(sketch, "E12.10.internal.snap0", {"position": v(0, 40.39) * mm});
            skFitSpline(sketch, "E12", {"points": [v(4.64, 48.34) * mm, v(6.7, 46.55) * mm, v(7.27, 44.3) * mm, v(8.43, 42.93) * mm, v(8.38, 37.82) * mm, v(6.2, 36.4) * mm, v(6.78, 33.23) * mm, v(5.94, 33.08) * mm, v(5.34, 36.62) * mm, v(2.92, 36.34) * mm, v(1.62, 40.39) * mm, v(3.53, 43.6) * mm, v(3.68, 46.5) * mm, v(4.64, 48.34) * mm]});
            skSolve(sketch);
        }
        {
            var Q0;
            Q0=makeQuery(id+"F11.imprint","IMPRINT",FACE,{"disambiguationData":[TD([[makeQuery(id+"F11.imprint","IMPRINT",EDGE,{"derivedFrom":sQuery(id+"F11.wireOp",EDGE,"E12")}),-1.0]])]});
            extrude(context, id + "F12", {"entities" : qUnion([Q0]), "operationType" : NewBodyOperationType.ADD, "depth" : 10 * mm});
        }
    });
